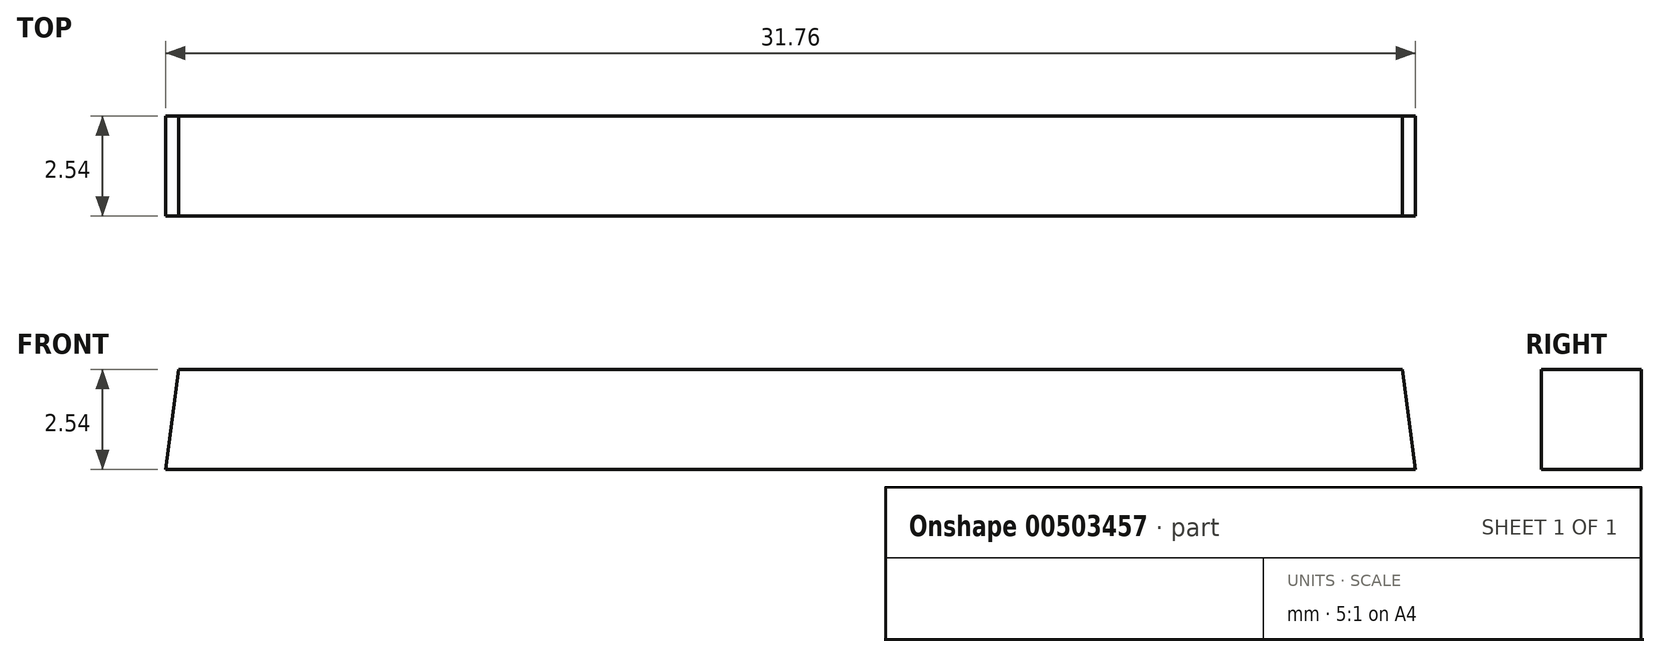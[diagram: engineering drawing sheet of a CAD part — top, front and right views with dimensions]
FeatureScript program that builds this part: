
annotation { "Feature Type Name" : "Feature", "Feature Type Description" : "" }
export const myFeature = defineFeature(function(context is Context, id is Id, definition is map)
    precondition{}
    {
        {
            var Q0;
            Q0=qCreatedBy(makeId("Front.planeOp"),FACE);
            var sketch = newSketch(context, id + "F0", { "sketchPlane" : qUnion([Q0])});
            skLineSegment(sketch, "E0", {"start": v(0, 0) * mm, "end": v(-15.87, 0) * mm});
            skLineSegment(sketch, "E1", {"start": v(-15.88, 0) * mm, "end": v(-15.54, 2.54) * mm});
            skLineSegment(sketch, "E2", {"start": v(-15.54, 2.54) * mm, "end": v(0, 2.54) * mm});
            skLineSegment(sketch, "E3.MirrorCS", {"start": v(0, 2.54) * mm, "end": v(0, 0) * mm});
            skLineSegment(sketch, "E4.MirrorCS", {"start": v(15.54, 2.54) * mm, "end": v(0, 2.54) * mm});
            skLineSegment(sketch, "E5.MirrorCS", {"start": v(15.88, 0) * mm, "end": v(15.54, 2.54) * mm});
            skLineSegment(sketch, "E6.MirrorCS", {"start": v(0, 0) * mm, "end": v(15.87, 0) * mm});
            skSolve(sketch);
        }
        {
            var Q0;
            Q0=makeQuery(id+"F0.imprint","IMPRINT",FACE,{"disambiguationData":[TD([[makeQuery(id+"F0.imprint","IMPRINT",EDGE,{"derivedFrom":sQuery(id+"F0.wireOp",EDGE,"E3.MirrorCS")}),1.0]])]});
            var Q1;
            Q1=makeQuery(id+"F0.imprint","IMPRINT",FACE,{"disambiguationData":[TD([[makeQuery(id+"F0.imprint","IMPRINT",EDGE,{"derivedFrom":sQuery(id+"F0.wireOp",EDGE,"E0")}),-1.0]])]});
            extrude(context, id + "F1", {"entities" : qUnion([Q0, Q1]), "depth" : 2.54 * mm, "offsetDistance" : 25.4 * mm, "symmetric" : true});
        }
    });
